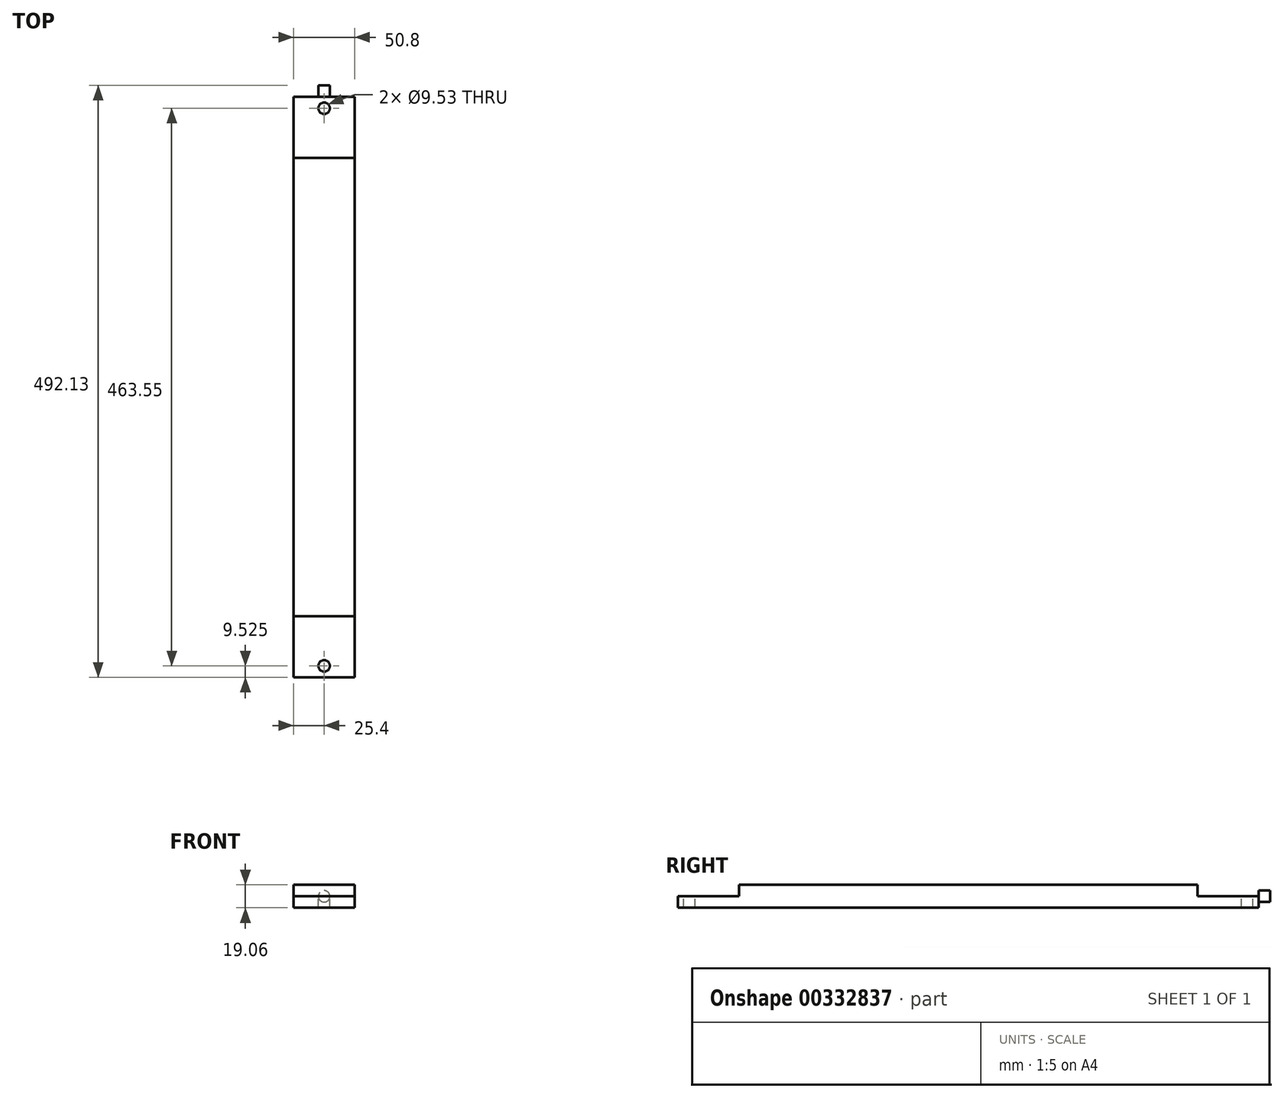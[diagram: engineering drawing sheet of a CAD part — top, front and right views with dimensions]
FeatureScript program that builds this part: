
annotation { "Feature Type Name" : "Feature", "Feature Type Description" : "" }
export const myFeature = defineFeature(function(context is Context, id is Id, definition is map)
    precondition{}
    {
        {
            var Q0;
            Q0=qCreatedBy(makeId("Right.planeOp"),FACE);
            var sketch = newSketch(context, id + "F0", { "sketchPlane" : qUnion([Q0])});
            skLineSegment(sketch, "E0", {"start": v(482.6, -9.52) * mm, "end": v(0, -9.52) * mm});
            skLineSegment(sketch, "E1.bottom", {"start": v(482.6, 9.53) * mm, "end": v(482.6, 0) * mm});
            skLineSegment(sketch, "E1.top", {"start": v(431.8, 9.53) * mm, "end": v(431.8, 0) * mm});
            skLineSegment(sketch, "E1.right", {"start": v(482.6, 0) * mm, "end": v(431.8, 0) * mm});
            skLineSegment(sketch, "E2.top", {"start": v(0, 9.53) * mm, "end": v(0, 0) * mm});
            skLineSegment(sketch, "E2.right", {"start": v(50.8, 0) * mm, "end": v(0, 0) * mm});
            skLineSegment(sketch, "E3", {"start": v(50.8, 0) * mm, "end": v(50.8, 9.53) * mm});
            skLineSegment(sketch, "E4.trimOffspring", {"start": v(50.8, 9.53) * mm, "end": v(431.8, 9.53) * mm});
            skLineSegment(sketch, "E5", {"start": v(0, 0) * mm, "end": v(0, -9.52) * mm});
            skLineSegment(sketch, "E6", {"start": v(482.6, 0) * mm, "end": v(482.6, -9.52) * mm});
            skSolve(sketch);
        }
        {
            var Q0;
            Q0=qSketchRegion(id+"F0",true);
            extrude(context, id + "F1", {"entities" : qUnion([Q0]), "endBound" : BoundingType.SYMMETRIC, "depth" : 50.8 * mm});
        }
        {
            var Q0;
            Q0=qCreatedBy(makeId("Top.planeOp"),FACE);
            var sketch = newSketch(context, id + "F2", { "sketchPlane" : qUnion([Q0])});
            skCircle(sketch, "E7", {"center": v(0, 9.53) * mm, "radius": 4.76 * mm});
            skCircle(sketch, "E8", {"center": v(0, 473.07) * mm, "radius": 4.76 * mm});
            skSolve(sketch);
        }
        {
            var Q0;
            Q0 = qSketchRegion(id + "F2", true);
            extrude(context, id + "F3", {"entities" : qUnion([Q0]), "operationType" : NewBodyOperationType.REMOVE, "oppositeDirection" : true, "depth" : 25.4 * mm});
        }
        {
            var Q0;
            Q0=qCreatedBy(makeId("Front.planeOp"),FACE);
            cPlane(context, id + "F4", {"entities" : qUnion([Q0]), "cplaneType" : CPlaneType.OFFSET, "offset" : 482.6 * mm, "oppositeDirection" : true, "width" : 152.4 * mm, "height" : 152.4 * mm});
        }
        {
            var Q0;
            Q0=qCreatedBy(id+"F4.planeOp",FACE);
            var sketch = newSketch(context, id + "F5", { "sketchPlane" : qUnion([Q0])});
            skCircle(sketch, "E9", {"center": v(0, 0) * mm, "radius": 4.76 * mm});
            skSolve(sketch);
        }
        {
            var Q0;
            Q0 = qSketchRegion(id + "F5", true);
            extrude(context, id + "F6", {"entities" : qUnion([Q0]), "operationType" : NewBodyOperationType.ADD, "oppositeDirection" : true, "depth" : 9.52 * mm});
        }
    });
